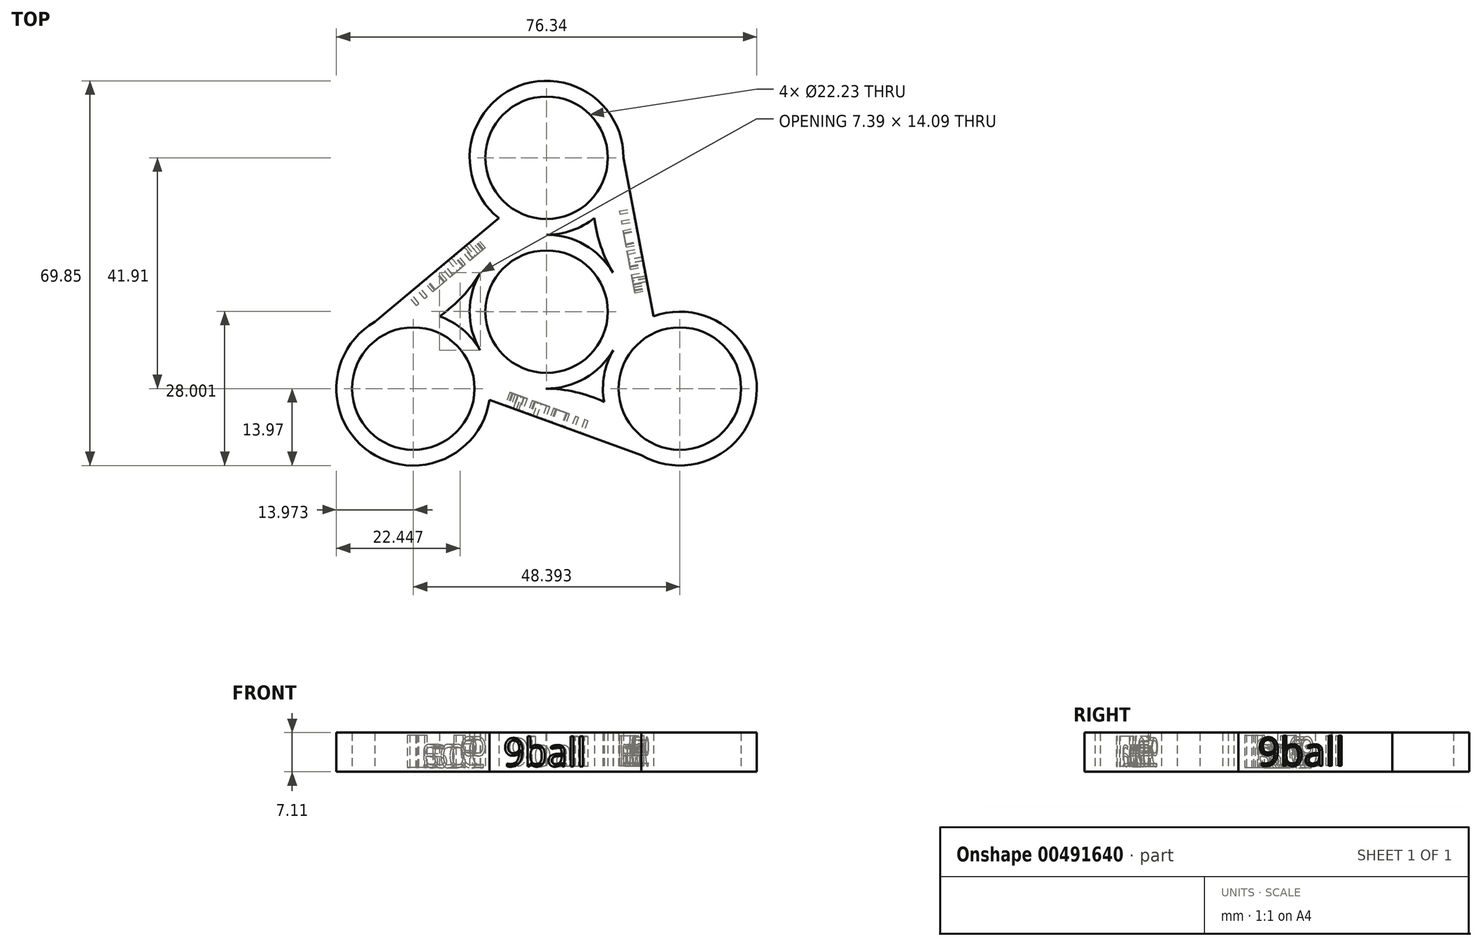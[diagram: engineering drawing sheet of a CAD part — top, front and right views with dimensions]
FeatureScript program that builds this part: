
annotation { "Feature Type Name" : "Feature", "Feature Type Description" : "" }
export const myFeature = defineFeature(function(context is Context, id is Id, definition is map)
    precondition{}
    {
        {
            var Q0;
            Q0=qCreatedBy(makeId("Top.planeOp"),FACE);
            var sketch = newSketch(context, id + "F0", { "sketchPlane" : qUnion([Q0])});
            skCircle(sketch, "E0", {"center": v(0, 0) * mm, "radius": 11.11 * mm});
            skCircle(sketch, "E1", {"center": v(0, 0) * mm, "radius": 13.97 * mm});
            skLineSegment(sketch, "E2", {"start": v(0, 0) * mm, "end": v(0, 27.94) * mm});
            skCircle(sketch, "E3", {"center": v(0, 27.94) * mm, "radius": 13.97 * mm});
            skCircle(sketch, "E4", {"center": v(0, 27.94) * mm, "radius": 11.11 * mm});
            skLineSegment(sketch, "E5", {"start": v(0, 0) * mm, "end": v(-24.2, -13.97) * mm});
            skLineSegment(sketch, "E6", {"start": v(0, 0) * mm, "end": v(24.2, -13.97) * mm});
            skCircle(sketch, "E7", {"center": v(-24.2, -13.97) * mm, "radius": 13.97 * mm});
            skCircle(sketch, "E8", {"center": v(-24.2, -13.97) * mm, "radius": 11.11 * mm});
            skCircle(sketch, "E9", {"center": v(24.2, -13.97) * mm, "radius": 13.97 * mm});
            skCircle(sketch, "E10", {"center": v(24.2, -13.97) * mm, "radius": 11.11 * mm});
            skLineSegment(sketch, "E11", {"start": v(0, 27.94) * mm, "end": v(-13.97, 27.94) * mm});
            skLineSegment(sketch, "E12", {"start": v(-24.2, -13.97) * mm, "end": v(-17.21, -26.07) * mm});
            skLineSegment(sketch, "E13", {"start": v(24.2, -13.97) * mm, "end": v(17.21, -26.07) * mm});
            skLineSegment(sketch, "E14", {"start": v(-12.1, -6.99) * mm, "end": v(-24.2, -13.97) * mm});
            skLineSegment(sketch, "E15", {"start": v(-24.2, -13.97) * mm, "end": v(-31.18, -1.87) * mm});
            skLineSegment(sketch, "E16", {"start": v(24.2, -13.97) * mm, "end": v(31.18, -1.87) * mm});
            skLineSegment(sketch, "E17", {"start": v(0, 27.94) * mm, "end": v(13.97, 27.94) * mm});
            skLineSegment(sketch, "E18", {"start": v(-24.2, -13.97) * mm, "end": v(-19.42, -0.84) * mm});
            skLineSegment(sketch, "E19", {"start": v(-8.68, 17) * mm, "end": v(0, 27.94) * mm});
            skArc(sketch, "E20", {"start": v(-19.42, -0.84) * mm, "mid": v(-12.14, 6.92) * mm, "end": v(-8.68, 17) * mm});
            skLineSegment(sketch, "E21", {"start": v(-24.2, -13.97) * mm, "end": v(-24.2, 0) * mm});
            skPoint(sketch, "E22.endSnap0", {"position": v(-4.34, 22.47) * mm});
            skArc(sketch, "E23.MirrorCS", {"start": v(19.42, -0.84) * mm, "mid": v(12.14, 6.92) * mm, "end": v(8.68, 17) * mm});
            skArc(sketch, "E24.MirrorCS", {"start": v(10.44, -16.4) * mm, "mid": v(0.07, -13.97) * mm, "end": v(-10.38, -16.01) * mm});
            skLineSegment(sketch, "E25", {"start": v(13.97, 27.94) * mm, "end": v(19.42, -0.84) * mm});
            skLineSegment(sketch, "E26", {"start": v(17.21, -26.07) * mm, "end": v(-10.38, -16.01) * mm});
            skLineSegment(sketch, "E27", {"start": v(-31.18, -1.87) * mm, "end": v(-8.68, 17) * mm});
            skSolve(sketch);
        }
        {
            var Q0;
            {var subQ0=sQuery(id+"F0.wireOp",EDGE,"E11");var subQ5=sQuery(id+"F0.wireOp",EDGE,"E4");var subQ6=makeQuery(id+"F0.imprint","INTERSECT",VERTEX,{"derivedFrom":[subQ5,subQ0]});Q0=makeQuery(id+"F0.imprint","IMPRINT",FACE,{"disambiguationData":[TD([[makeQuery(id+"F0.imprint","IMPRINT",EDGE,{"disambiguationData":[TD([[subQ6,1.0]])],"derivedFrom":subQ5}),-1.0]])]});}
            var Q1;
            {var subQ3=sQuery(id+"F0.wireOp",EDGE,"E15");var subQ5=sQuery(id+"F0.wireOp",EDGE,"E8");var subQ6=makeQuery(id+"F0.imprint","INTERSECT",VERTEX,{"derivedFrom":[subQ5,subQ3]});Q1=makeQuery(id+"F0.imprint","IMPRINT",FACE,{"disambiguationData":[TD([[makeQuery(id+"F0.imprint","IMPRINT",EDGE,{"disambiguationData":[TD([[subQ6,-1.0]])],"derivedFrom":subQ5}),-1.0]])]});}
            var Q2;
            {var subQ3=sQuery(id+"F0.wireOp",EDGE,"E16");var subQ5=sQuery(id+"F0.wireOp",EDGE,"E10");var subQ6=makeQuery(id+"F0.imprint","INTERSECT",VERTEX,{"derivedFrom":[subQ5,subQ3]});Q2=makeQuery(id+"F0.imprint","IMPRINT",FACE,{"disambiguationData":[TD([[makeQuery(id+"F0.imprint","IMPRINT",EDGE,{"disambiguationData":[TD([[subQ6,1.0]])],"derivedFrom":subQ5}),-1.0]])]});}
            var Q3;
            {var subQ0=sQuery(id+"F0.wireOp",EDGE,"E11");var subQ5=sQuery(id+"F0.wireOp",EDGE,"E4");var subQ6=makeQuery(id+"F0.imprint","INTERSECT",VERTEX,{"derivedFrom":[subQ5,subQ0]});Q3=makeQuery(id+"F0.imprint","IMPRINT",FACE,{"disambiguationData":[TD([[makeQuery(id+"F0.imprint","IMPRINT",EDGE,{"disambiguationData":[TD([[subQ6,-1.0]])],"derivedFrom":subQ5}),-1.0]])]});}
            var Q4;
            {var subQ3=sQuery(id+"F0.wireOp",EDGE,"E21");var subQ5=sQuery(id+"F0.wireOp",EDGE,"E8");var subQ7=makeQuery(id+"F0.imprint","INTERSECT",VERTEX,{"derivedFrom":[subQ5,subQ3]});Q4=makeQuery(id+"F0.imprint","IMPRINT",FACE,{"disambiguationData":[TD([[makeQuery(id+"F0.imprint","IMPRINT",EDGE,{"disambiguationData":[TD([[subQ7,-1.0]])],"derivedFrom":subQ5}),-1.0]])]});}
            var Q5;
            {var subQ1=sQuery(id+"F0.wireOp",EDGE,"E3");var subQ3=makeQuery(id+"F0.imprint","INTERSECT",VERTEX,{"derivedFrom":[subQ1,sQuery(id+"F0.wireOp",EDGE,"5e0eac27-506a-4d55-a6b8-50ddd9d8d8e10.MirrorCS")]});Q5=makeQuery(id+"F0.imprint","IMPRINT",FACE,{"disambiguationData":[TD([[makeQuery(id+"F0.imprint","IMPRINT",EDGE,{"disambiguationData":[TD([[subQ3,1.0]])],"derivedFrom":subQ1}),1.0]])]});}
            var Q6;
            {var subQ0=sQuery(id+"F0.wireOp",EDGE,"E9");var subQ6=makeQuery(id+"F0.imprint","INTERSECT",VERTEX,{"derivedFrom":[subQ0,sQuery(id+"F0.wireOp",EDGE,"5e0eac27-506a-4d55-a6b8-50ddd9d8d8e10.MirrorCS")]});Q6=makeQuery(id+"F0.imprint","IMPRINT",FACE,{"disambiguationData":[TD([[makeQuery(id+"F0.imprint","IMPRINT",EDGE,{"disambiguationData":[TD([[subQ6,-1.0]])],"derivedFrom":subQ0}),1.0]])]});}
            var Q7;
            {var subQ1=sQuery(id+"F0.wireOp",EDGE,"E9");var subQ4=makeQuery(id+"F0.imprint","INTERSECT",VERTEX,{"derivedFrom":[subQ1,sQuery(id+"F0.wireOp",EDGE,"E24.MirrorCS")]});Q7=makeQuery(id+"F0.imprint","IMPRINT",FACE,{"disambiguationData":[TD([[makeQuery(id+"F0.imprint","IMPRINT",EDGE,{"disambiguationData":[TD([[subQ4,-1.0]])],"derivedFrom":subQ1}),1.0]])]});}
            var Q8;
            {var subQ5=sQuery(id+"F0.wireOp",EDGE,"E7");var subQ7=makeQuery(id+"F0.imprint","INTERSECT",VERTEX,{"derivedFrom":[subQ5,sQuery(id+"F0.wireOp",EDGE,"E24.MirrorCS")]});Q8=makeQuery(id+"F0.imprint","IMPRINT",FACE,{"disambiguationData":[TD([[makeQuery(id+"F0.imprint","IMPRINT",EDGE,{"disambiguationData":[TD([[subQ7,1.0]])],"derivedFrom":subQ5}),1.0]])]});}
            var Q9;
            {var subQ0=sQuery(id+"F0.wireOp",EDGE,"E4");var subQ1=sQuery(id+"F0.wireOp",EDGE,"E2");var subQ2=makeQuery(id+"F0.imprint","INTERSECT",VERTEX,{"derivedFrom":[subQ1,subQ0]});Q9=makeQuery(id+"F0.imprint","IMPRINT",FACE,{"disambiguationData":[TD([[makeQuery(id+"F0.imprint","IMPRINT",EDGE,{"disambiguationData":[TD([[subQ2,1.0]])],"derivedFrom":subQ0}),-1.0]])]});}
            var Q10;
            {var subQ3=sQuery(id+"F0.wireOp",EDGE,"OxELbnh2-pf1s-LPYb-cjNd-jSZVnj8Dmi9T");var subQ5=sQuery(id+"F0.wireOp",EDGE,"E4");var subQ6=makeQuery(id+"F0.imprint","INTERSECT",VERTEX,{"derivedFrom":[subQ5,subQ3]});Q10=makeQuery(id+"F0.imprint","IMPRINT",FACE,{"disambiguationData":[TD([[makeQuery(id+"F0.imprint","IMPRINT",EDGE,{"disambiguationData":[TD([[subQ6,-1.0]])],"derivedFrom":subQ5}),-1.0]])]});}
            var Q11;
            {var subQ4=sQuery(id+"F0.wireOp",EDGE,"5e0eac27-506a-4d55-a6b8-50ddd9d8d8e10.MirrorCS");Q11=makeQuery(id+"F0.imprint","IMPRINT",FACE,{"disambiguationData":[TD([[makeQuery(id+"F0.imprint","IMPRINT",EDGE,{"derivedFrom":subQ4}),1.0]])]});}
            var Q12;
            {var subQ4=sQuery(id+"F0.wireOp",EDGE,"wTarZKbT-j9Fz-NUgE-Mupu-ReBFeg8jicUt");Q12=makeQuery(id+"F0.imprint","IMPRINT",FACE,{"disambiguationData":[TD([[makeQuery(id+"F0.imprint","IMPRINT",EDGE,{"derivedFrom":subQ4}),-1.0]])]});}
            var Q13;
            {var subQ6=sQuery(id+"F0.wireOp",EDGE,"fd0ed326-dc61-4633-886d-73886feb56c90.MirrorCS");Q13=makeQuery(id+"F0.imprint","IMPRINT",FACE,{"disambiguationData":[TD([[makeQuery(id+"F0.imprint","IMPRINT",EDGE,{"derivedFrom":subQ6}),-1.0]])]});}
            var Q14;
            {var subQ4=sQuery(id+"F0.wireOp",EDGE,"E5");var subQ6=sQuery(id+"F0.wireOp",EDGE,"E0");var subQ7=makeQuery(id+"F0.imprint","INTERSECT",VERTEX,{"derivedFrom":[subQ6,subQ4]});Q14=makeQuery(id+"F0.imprint","IMPRINT",FACE,{"disambiguationData":[TD([[makeQuery(id+"F0.imprint","IMPRINT",EDGE,{"disambiguationData":[TD([[subQ7,-1.0]])],"derivedFrom":subQ6}),-1.0]])]});}
            var Q15;
            {var subQ4=sQuery(id+"F0.wireOp",EDGE,"E5");var subQ6=sQuery(id+"F0.wireOp",EDGE,"E0");var subQ7=makeQuery(id+"F0.imprint","INTERSECT",VERTEX,{"derivedFrom":[subQ6,subQ4]});Q15=makeQuery(id+"F0.imprint","IMPRINT",FACE,{"disambiguationData":[TD([[makeQuery(id+"F0.imprint","IMPRINT",EDGE,{"disambiguationData":[TD([[subQ7,1.0]])],"derivedFrom":subQ6}),-1.0]])]});}
            var Q16;
            {var subQ0=sQuery(id+"F0.wireOp",EDGE,"E2");var subQ1=sQuery(id+"F0.wireOp",EDGE,"E0");var subQ2=makeQuery(id+"F0.imprint","INTERSECT",VERTEX,{"derivedFrom":[subQ1,subQ0]});Q16=makeQuery(id+"F0.imprint","IMPRINT",FACE,{"disambiguationData":[TD([[makeQuery(id+"F0.imprint","IMPRINT",EDGE,{"disambiguationData":[TD([[subQ2,1.0]])],"derivedFrom":subQ1}),-1.0]])]});}
            var Q17;
            {var subQ0=sQuery(id+"F0.wireOp",EDGE,"E18");var subQ5=sQuery(id+"F0.wireOp",EDGE,"E8");var subQ7=makeQuery(id+"F0.imprint","INTERSECT",VERTEX,{"derivedFrom":[subQ5,subQ0]});Q17=makeQuery(id+"F0.imprint","IMPRINT",FACE,{"disambiguationData":[TD([[makeQuery(id+"F0.imprint","IMPRINT",EDGE,{"disambiguationData":[TD([[subQ7,-1.0]])],"derivedFrom":subQ5}),-1.0]])]});}
            var Q18;
            {var subQ3=sQuery(id+"F0.wireOp",EDGE,"E18");var subQ5=sQuery(id+"F0.wireOp",EDGE,"E8");var subQ6=makeQuery(id+"F0.imprint","INTERSECT",VERTEX,{"derivedFrom":[subQ5,subQ3]});Q18=makeQuery(id+"F0.imprint","IMPRINT",FACE,{"disambiguationData":[TD([[makeQuery(id+"F0.imprint","IMPRINT",EDGE,{"disambiguationData":[TD([[subQ6,1.0]])],"derivedFrom":subQ5}),-1.0]])]});}
            var Q19;
            {var subQ4=sQuery(id+"F0.wireOp",EDGE,"E4");var subQ5=sQuery(id+"F0.wireOp",EDGE,"E2");var subQ6=makeQuery(id+"F0.imprint","INTERSECT",VERTEX,{"derivedFrom":[subQ5,subQ4]});Q19=makeQuery(id+"F0.imprint","IMPRINT",FACE,{"disambiguationData":[TD([[makeQuery(id+"F0.imprint","IMPRINT",EDGE,{"disambiguationData":[TD([[subQ6,-1.0]])],"derivedFrom":subQ4}),-1.0]])]});}
            var Q20;
            {var subQ0=sQuery(id+"F0.wireOp",EDGE,"E25");Q20=makeQuery(id+"F0.imprint","IMPRINT",FACE,{"disambiguationData":[TD([[makeQuery(id+"F0.imprint","IMPRINT",EDGE,{"derivedFrom":subQ0}),-1.0]])]});}
            var Q21;
            {var subQ0=sQuery(id+"F0.wireOp",EDGE,"E27");Q21=makeQuery(id+"F0.imprint","IMPRINT",FACE,{"disambiguationData":[TD([[makeQuery(id+"F0.imprint","IMPRINT",EDGE,{"derivedFrom":subQ0}),-1.0]])]});}
            var Q22;
            {var subQ0=sQuery(id+"F0.wireOp",EDGE,"E26");Q22=makeQuery(id+"F0.imprint","IMPRINT",FACE,{"disambiguationData":[TD([[makeQuery(id+"F0.imprint","IMPRINT",EDGE,{"derivedFrom":subQ0}),-1.0]])]});}
            var Q23;
            {var subQ0=sQuery(id+"F0.wireOp",EDGE,"E20");var subQ1=sQuery(id+"F0.wireOp",EDGE,"E1");var subQ2=makeQuery(id+"F0.imprint","INTERSECT",VERTEX,{"derivedFrom":[subQ1,subQ0]});Q23=makeQuery(id+"F0.imprint","IMPRINT",FACE,{"disambiguationData":[TD([[makeQuery(id+"F0.imprint","IMPRINT",EDGE,{"disambiguationData":[TD([[subQ2,1.0]])],"derivedFrom":subQ1}),-1.0]])]});}
            var Q24;
            {var subQ0=sQuery(id+"F0.wireOp",EDGE,"E23.MirrorCS");var subQ1=sQuery(id+"F0.wireOp",EDGE,"E1");var subQ2=makeQuery(id+"F0.imprint","INTERSECT",VERTEX,{"derivedFrom":[subQ1,subQ0]});Q24=makeQuery(id+"F0.imprint","IMPRINT",FACE,{"disambiguationData":[TD([[makeQuery(id+"F0.imprint","IMPRINT",EDGE,{"disambiguationData":[TD([[subQ2,1.0]])],"derivedFrom":subQ1}),-1.0]])]});}
            var Q25;
            {var subQ1=sQuery(id+"F0.wireOp",EDGE,"E1");var subQ3=sQuery(id+"F0.wireOp",EDGE,"E24.MirrorCS");var subQ4=makeQuery(id+"F0.imprint","INTERSECT",VERTEX,{"derivedFrom":[subQ1,subQ3]});Q25=makeQuery(id+"F0.imprint","IMPRINT",FACE,{"disambiguationData":[TD([[makeQuery(id+"F0.imprint","IMPRINT",EDGE,{"disambiguationData":[TD([[subQ4,-1.0]])],"derivedFrom":subQ3}),-1.0]])]});}
            extrude(context, id + "F1", {"entities" : qUnion([Q0, Q1, Q2, Q3, Q4, Q5, Q6, Q7, Q8, Q9, Q10, Q11, Q12, Q13, Q14, Q15, Q16, Q17, Q18, Q19, Q20, Q21, Q22, Q23, Q24, Q25]), "depth" : 7.11 * mm});
        }
        {
            var Q0;
            Q0=makeQuery(id+"F1.opExtrude","SWEPT_FACE",FACE,{"disambiguationData":[OSD([sQuery(id+"F0.wireOp",EDGE,"E25")])]});
            var sketch = newSketch(context, id + "F2", { "sketchPlane" : qUnion([Q0])});
            skPoint(sketch, "E28.secondSnap0", {"position": v(10.2, 7.11) * mm});
            skText(sketch, "E29", { "text": "9ball\n", "fontName": "OpenSans-Regular.ttf"});
            const initialGuessF2  = {"E29": [0, 0.0011, 1, 0, 0.00516]};
            skSetInitialGuess(sketch, initialGuessF2);
            skSolve(sketch);
        }
        {
            var Q0;
            Q0=qSketchRegion(id+"F2",true);
            extrude(context, id + "F3", {"entities" : qUnion([Q0]), "operationType" : NewBodyOperationType.REMOVE, "oppositeDirection" : true, "depth" : 2.54 * mm});
        }
        {
            var Q0;
            Q0=makeQuery(id+"F1.opExtrude","SWEPT_FACE",FACE,{"disambiguationData":[OSD([sQuery(id+"F0.wireOp",EDGE,"E26")])]});
            var sketch = newSketch(context, id + "F4", { "sketchPlane" : qUnion([Q0])});
            skText(sketch, "E30", { "text": "9ball\n", "fontName": "OpenSans-Regular.ttf"});
            const initialGuessF4  = {"E30": [-0.0016, 0.001, 1, 0, 0.00513]};
            skSetInitialGuess(sketch, initialGuessF4);
            skSolve(sketch);
        }
        {
            var Q0;
            Q0 = qSketchRegion(id + "F4", true);
            extrude(context, id + "F5", {"entities" : qUnion([Q0]), "operationType" : NewBodyOperationType.REMOVE, "oppositeDirection" : true, "depth" : 2.54 * mm});
        }
        {
            var Q0;
            Q0=makeQuery(id+"F1.opExtrude","SWEPT_FACE",FACE,{"disambiguationData":[OSD([sQuery(id+"F0.wireOp",EDGE,"E27")])]});
            var sketch = newSketch(context, id + "F6", { "sketchPlane" : qUnion([Q0])});
            skText(sketch, "E31", { "text": "9ball\n", "fontName": "OpenSans-Regular.ttf"});
            const initialGuessF6  = {"E31": [0.00069, 0.00078, 1, 0, 0.00557]};
            skSetInitialGuess(sketch, initialGuessF6);
            skSolve(sketch);
        }
        {
            var Q0;
            Q0 = qSketchRegion(id + "F6", true);
            extrude(context, id + "F7", {"entities" : qUnion([Q0]), "operationType" : NewBodyOperationType.REMOVE, "oppositeDirection" : true, "depth" : 2.54 * mm});
        }
    });
